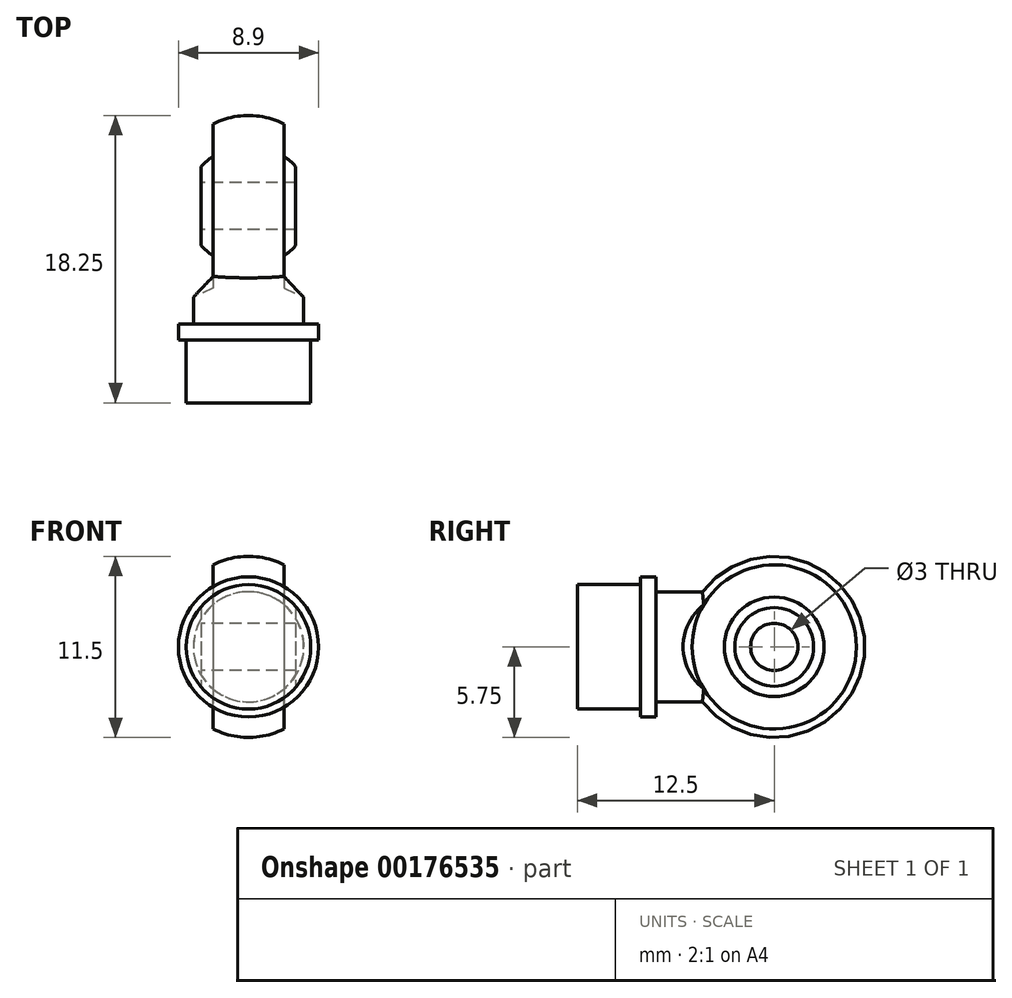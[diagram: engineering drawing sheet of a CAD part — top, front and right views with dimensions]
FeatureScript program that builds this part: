
annotation { "Feature Type Name" : "Feature", "Feature Type Description" : "" }
export const myFeature = defineFeature(function(context is Context, id is Id, definition is map)
    precondition{}
    {
        {
            var Q0;
            Q0=qCreatedBy(makeId("Top.planeOp"),FACE);
            var sketch = newSketch(context, id + "F0", { "sketchPlane" : qUnion([Q0])});
            skLineSegment(sketch, "E0", {"start": v(-3, 0) * mm, "end": v(3, 0) * mm, "construction": true});
            skLineSegment(sketch, "E1", {"start": v(-3, 1.5) * mm, "end": v(-3, 2.5) * mm});
            skLineSegment(sketch, "E2", {"start": v(-3, 1.5) * mm, "end": v(3, 1.5) * mm});
            skLineSegment(sketch, "E3", {"start": v(3, 1.5) * mm, "end": v(3, 2.5) * mm});
            skLineSegment(sketch, "E4", {"start": v(-2.25, 3.16) * mm, "end": v(-2.25, 5.22) * mm});
            skArc(sketch, "E5", {"start": v(2.25, 5.22) * mm, "mid": v(0, 5.75) * mm, "end": v(-2.25, 5.22) * mm});
            skLineSegment(sketch, "E6", {"start": v(2.25, 5.22) * mm, "end": v(2.25, 3.16) * mm});
            skLineSegment(sketch, "E7", {"start": v(0, 0) * mm, "end": v(0, 5.75) * mm, "construction": true});
            skLineSegment(sketch, "E8", {"start": v(2.25, 5.22) * mm, "end": v(3.95, 6) * mm});
            skLineSegment(sketch, "E9", {"start": v(3.95, 6) * mm, "end": v(5, 6) * mm});
            skLineSegment(sketch, "E10", {"start": v(5, 6) * mm, "end": v(5, 1.5) * mm});
            skLineSegment(sketch, "E11", {"start": v(5, 1.5) * mm, "end": v(3, 1.5) * mm});
            skLineSegment(sketch, "E12.MirrorCS", {"start": v(-2.25, 5.22) * mm, "end": v(-3.95, 6) * mm});
            skLineSegment(sketch, "E13.MirrorCS", {"start": v(-3.95, 6) * mm, "end": v(-5, 6) * mm});
            skLineSegment(sketch, "E14.MirrorCS", {"start": v(-5, 6) * mm, "end": v(-5, 1.5) * mm});
            skLineSegment(sketch, "E15.MirrorCS", {"start": v(-5, 1.5) * mm, "end": v(-3, 1.5) * mm});
            skArc(sketch, "E16", {"start": v(3, 2.5) * mm, "mid": v(0, 3.85) * mm, "end": v(-3, 2.5) * mm});
            skSolve(sketch);
        }
        {
            var Q0;
            {var subQ1=sQuery(id+"F0.wireOp",EDGE,"E1");Q0=makeQuery(id+"F0.imprint","IMPRINT",FACE,{"disambiguationData":[TD([[makeQuery(id+"F0.imprint","IMPRINT",EDGE,{"derivedFrom":subQ1}),-1.0]])]});}
            var Q1;
            {var subQ0=sQuery(id+"F0.wireOp",EDGE,"E4");Q1=makeQuery(id+"F0.imprint","IMPRINT",FACE,{"disambiguationData":[TD([[makeQuery(id+"F0.imprint","IMPRINT",EDGE,{"derivedFrom":subQ0}),-1.0]])]});}
            var Q2;
            Q2=sQuery(id+"F0.wireOp",EDGE,"E0");
            revolve(context, id + "F1", {"entities" : qUnion([Q0, Q1]), "axis" : qUnion([Q2]), "revolveType" : RevolveType.FULL});
        }
        {
            var Q0;
            Q0=qCreatedBy(makeId("Right.planeOp"),FACE);
            var sketch = newSketch(context, id + "F2", { "sketchPlane" : qUnion([Q0])});
            skLineSegment(sketch, "E17", {"start": v(0, 0) * mm, "end": v(-12.5, 0) * mm, "construction": true});
            skLineSegment(sketch, "E18", {"start": v(-12.5, 0) * mm, "end": v(-12.5, 3.95) * mm});
            skLineSegment(sketch, "E19", {"start": v(-12.5, 3.95) * mm, "end": v(-8.5, 3.95) * mm});
            skLineSegment(sketch, "E20", {"start": v(-8.5, 3.95) * mm, "end": v(-8.5, 4.45) * mm});
            skLineSegment(sketch, "E21", {"start": v(-8.5, 4.45) * mm, "end": v(-7.5, 4.45) * mm});
            skLineSegment(sketch, "E22", {"start": v(-7.5, 4.45) * mm, "end": v(-7.5, 3.5) * mm});
            skLineSegment(sketch, "E23", {"start": v(-7.5, 3.5) * mm, "end": v(-3, 3.5) * mm});
            skLineSegment(sketch, "E24", {"start": v(-3, 3.5) * mm, "end": v(-3, 0) * mm});
            skLineSegment(sketch, "E25", {"start": v(-3, 0) * mm, "end": v(-12.5, 0) * mm});
            skSolve(sketch);
        }
        {
            var Q0;
            Q0=makeQuery(id+"F2.imprint","IMPRINT",FACE,{"disambiguationData":[TD([[makeQuery(id+"F2.imprint","IMPRINT",EDGE,{"derivedFrom":sQuery(id+"F2.wireOp",EDGE,"E18")}),-1.0]])]});
            var Q1;
            Q1=sQuery(id+"F2.wireOp",EDGE,"E17");
            revolve(context, id + "F3", {"operationType" : NewBodyOperationType.ADD, "entities" : qUnion([Q0]), "axis" : qUnion([Q1]), "revolveType" : RevolveType.FULL});
        }
        {
            var Q0;
            {var subQ1=sQuery(id+"F0.wireOp",EDGE,"E3");Q0=makeQuery(id+"F0.imprint","IMPRINT",FACE,{"disambiguationData":[TD([[makeQuery(id+"F0.imprint","IMPRINT",EDGE,{"derivedFrom":subQ1}),-1.0]])]});}
            var Q1;
            {var subQ2=sQuery(id+"F0.wireOp",EDGE,"E1");Q1=makeQuery(id+"F0.imprint","IMPRINT",FACE,{"disambiguationData":[TD([[makeQuery(id+"F0.imprint","IMPRINT",EDGE,{"derivedFrom":subQ2}),1.0]])]});}
            var Q2;
            Q2=sQuery(id+"F0.wireOp",EDGE,"E0");
            revolve(context, id + "F4", {"operationType" : NewBodyOperationType.REMOVE, "entities" : qUnion([Q0, Q1]), "axis" : qUnion([Q2]), "revolveType" : RevolveType.FULL, "oppositeDirection" : true});
        }
    });
